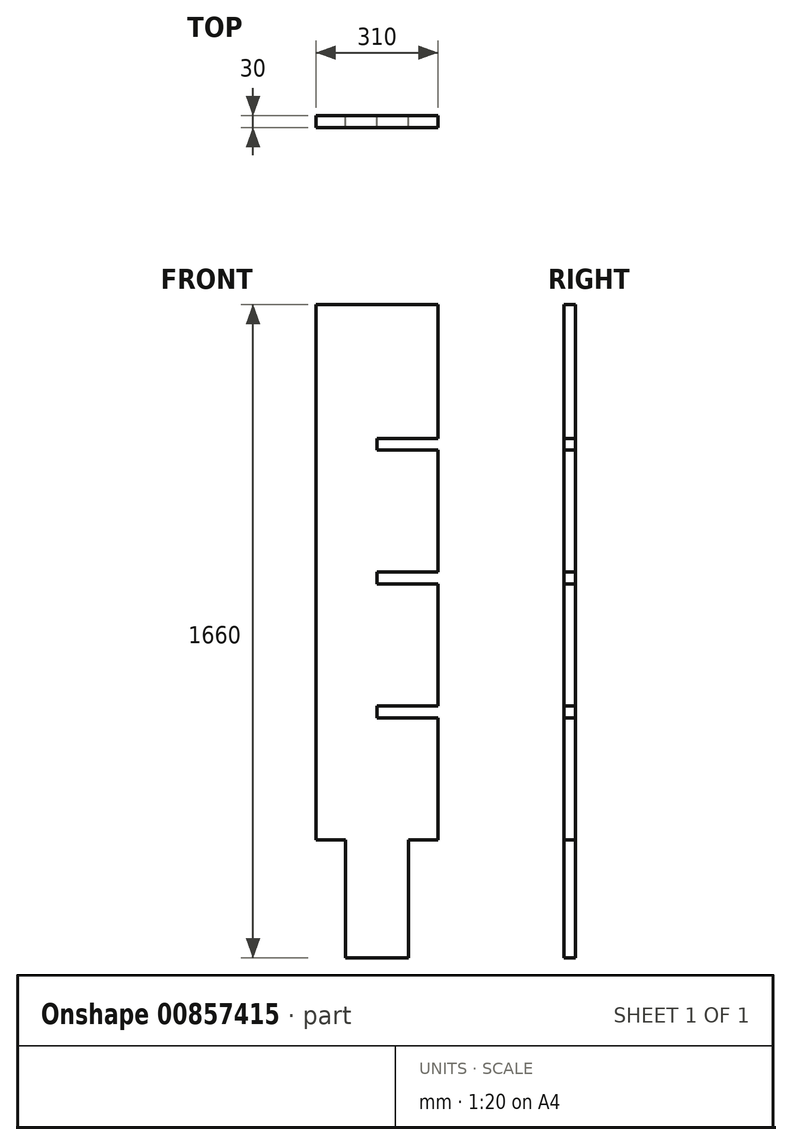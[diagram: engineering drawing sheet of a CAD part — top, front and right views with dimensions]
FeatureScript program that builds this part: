
annotation { "Feature Type Name" : "Feature", "Feature Type Description" : "" }
export const myFeature = defineFeature(function(context is Context, id is Id, definition is map)
    precondition{}
    {
        {
            var Q0;
            Q0=qCreatedBy(makeId("Front.planeOp"),FACE);
            var sketch = newSketch(context, id + "F0", { "sketchPlane" : qUnion([Q0])});
            skLineSegment(sketch, "E0", {"start": v(-80, -40.73) * mm, "end": v(-80, 259.27) * mm});
            skLineSegment(sketch, "E1", {"start": v(-80, 259.27) * mm, "end": v(-155, 259.27) * mm});
            skLineSegment(sketch, "E2", {"start": v(-155, 259.27) * mm, "end": v(-155, 1619.27) * mm});
            skLineSegment(sketch, "E3", {"start": v(-155, 1619.27) * mm, "end": v(155, 1619.27) * mm});
            skLineSegment(sketch, "E4", {"start": v(155, 1619.27) * mm, "end": v(155, 1279.27) * mm});
            skLineSegment(sketch, "E5", {"start": v(155, 1279.27) * mm, "end": v(0, 1279.27) * mm});
            skLineSegment(sketch, "E6", {"start": v(0, 1279.27) * mm, "end": v(0, 1249.27) * mm});
            skLineSegment(sketch, "E7", {"start": v(0, 1249.27) * mm, "end": v(155, 1249.27) * mm});
            skLineSegment(sketch, "E8", {"start": v(155, 1249.27) * mm, "end": v(155, 939.27) * mm});
            skLineSegment(sketch, "E9", {"start": v(155, 939.27) * mm, "end": v(0, 939.27) * mm});
            skLineSegment(sketch, "E10", {"start": v(0, 939.27) * mm, "end": v(0, 909.27) * mm});
            skLineSegment(sketch, "E11", {"start": v(0, 909.27) * mm, "end": v(155, 909.27) * mm});
            skLineSegment(sketch, "E12", {"start": v(155, 909.27) * mm, "end": v(155, 599.27) * mm});
            skLineSegment(sketch, "E13", {"start": v(155, 599.27) * mm, "end": v(0, 599.27) * mm});
            skLineSegment(sketch, "E14", {"start": v(0, 599.27) * mm, "end": v(0, 569.27) * mm});
            skLineSegment(sketch, "E15", {"start": v(0, 569.27) * mm, "end": v(155, 569.27) * mm});
            skLineSegment(sketch, "E16", {"start": v(155, 569.27) * mm, "end": v(155, 259.27) * mm});
            skLineSegment(sketch, "E17", {"start": v(155, 259.27) * mm, "end": v(80, 259.27) * mm});
            skLineSegment(sketch, "E18", {"start": v(-80, -40.73) * mm, "end": v(80, -40.73) * mm});
            skLineSegment(sketch, "E19", {"start": v(80, -40.73) * mm, "end": v(80, 259.27) * mm});
            skSolve(sketch);
        }
        {
            var Q0;
            Q0=makeQuery(id+"F0.imprint","IMPRINT",FACE,{"disambiguationData":[TD([[makeQuery(id+"F0.imprint","IMPRINT",EDGE,{"derivedFrom":sQuery(id+"F0.wireOp",EDGE,"E0")}),-1.0]])]});
            extrude(context, id + "F1", {"entities" : qUnion([Q0]), "depth" : 30 * mm, "offsetDistance" : 25 * mm});
        }
    });
